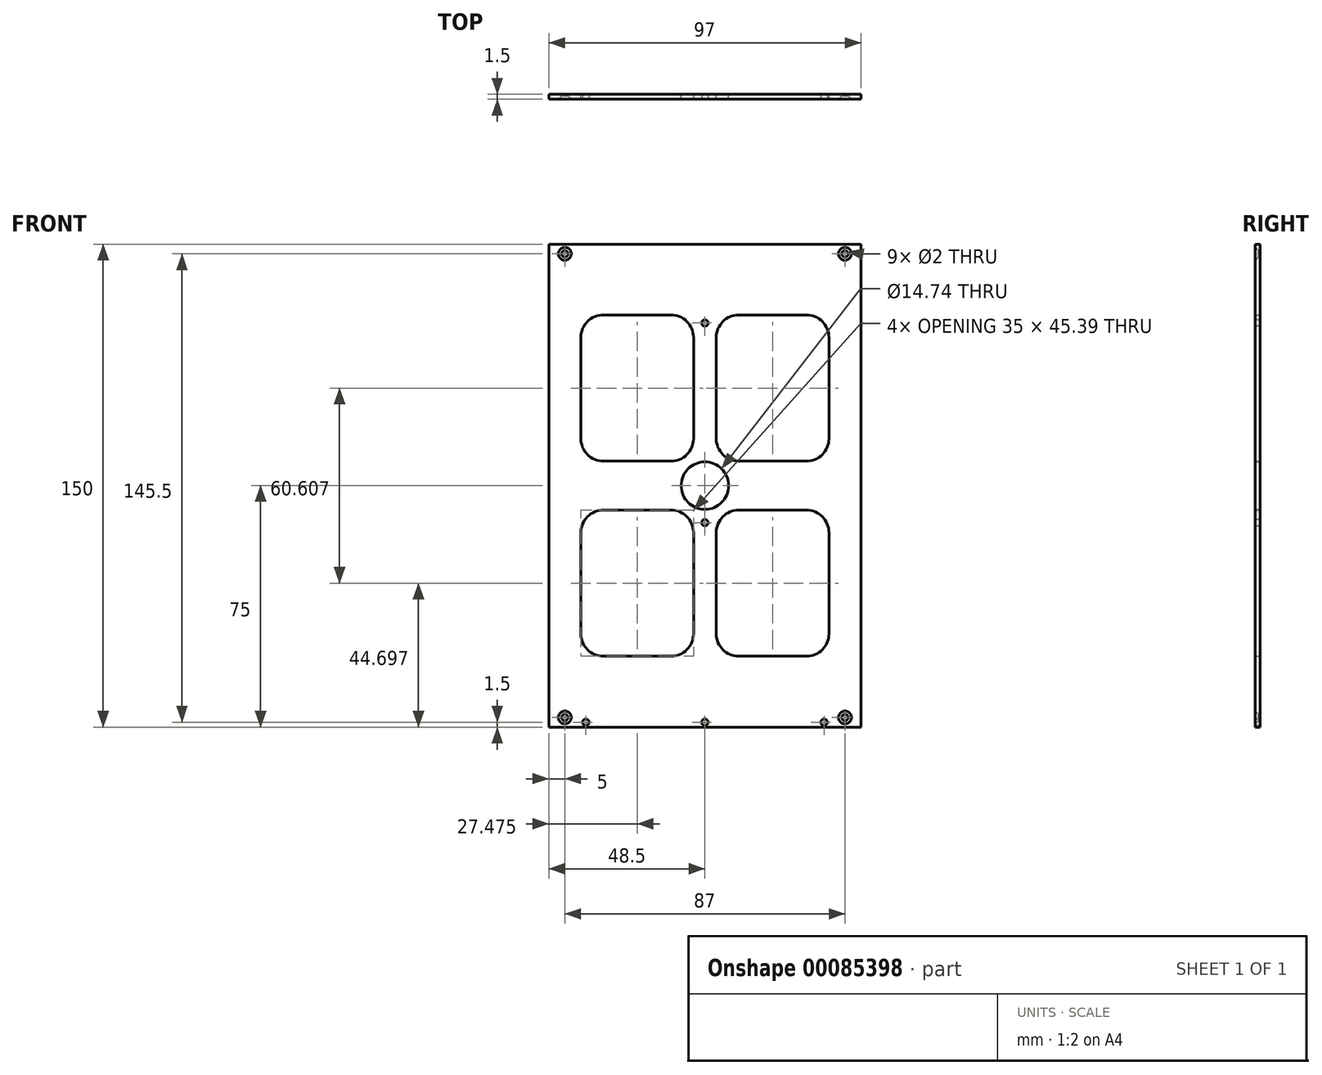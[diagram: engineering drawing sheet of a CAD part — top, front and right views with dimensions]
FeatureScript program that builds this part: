
annotation { "Feature Type Name" : "Feature", "Feature Type Description" : "" }
export const myFeature = defineFeature(function(context is Context, id is Id, definition is map)
    precondition{}
    {
        {
            var Q0;
            Q0=qCreatedBy(makeId("Front.planeOp"),FACE);
            var sketch = newSketch(context, id + "F0", { "sketchPlane" : qUnion([Q0])});
            skLineSegment(sketch, "E0.rect.bottom", {"start": v(-48.5, 75) * mm, "end": v(48.5, 75) * mm});
            skLineSegment(sketch, "E0.rect.top", {"start": v(-48.5, -75) * mm, "end": v(48.5, -75) * mm});
            skLineSegment(sketch, "E0.rect.left", {"start": v(-48.5, 75) * mm, "end": v(-48.5, -75) * mm});
            skLineSegment(sketch, "E0.rect.right", {"start": v(48.5, 75) * mm, "end": v(48.5, -75) * mm});
            skPoint(sketch, "E0.rect.middle", {"position": v(0, 0) * mm});
            skLineSegment(sketch, "E1.rect.bottom", {"start": v(-10.52, 7.6) * mm, "end": v(-31.52, 7.6) * mm});
            skLineSegment(sketch, "E1.rect.top", {"start": v(-10.52, 53) * mm, "end": v(-31.52, 53) * mm});
            skLineSegment(sketch, "E1.rect.left", {"start": v(-3.52, 14.6) * mm, "end": v(-3.52, 46) * mm});
            skLineSegment(sketch, "E1.rect.right", {"start": v(-38.52, 14.6) * mm, "end": v(-38.52, 46) * mm});
            skPoint(sketch, "E1.rect.middle", {"position": v(-21.02, 30.3) * mm});
            skPoint(sketch, "E2", {"position": v(0, 75) * mm});
            skPoint(sketch, "E3", {"position": v(-24.25, 75) * mm});
            skPoint(sketch, "E4.MirrorP", {"position": v(-24.25, -75) * mm});
            skPoint(sketch, "E5.visualSharp", {"position": v(-3.52, 7.6) * mm});
            skArc(sketch, "E5.filletArc", {"start": v(-10.52, 7.6) * mm, "mid": v(-5.58, 9.66) * mm, "end": v(-3.52, 14.6) * mm});
            skPoint(sketch, "E6.visualSharp", {"position": v(-3.52, 53) * mm});
            skArc(sketch, "E6.filletArc", {"start": v(-3.52, 46) * mm, "mid": v(-5.58, 50.95) * mm, "end": v(-10.52, 53) * mm});
            skPoint(sketch, "E7.visualSharp", {"position": v(-38.52, 53) * mm});
            skArc(sketch, "E7.filletArc", {"start": v(-31.52, 53) * mm, "mid": v(-36.47, 50.95) * mm, "end": v(-38.52, 46) * mm});
            skPoint(sketch, "E8.visualSharp", {"position": v(-38.52, 7.6) * mm});
            skArc(sketch, "E8.filletArc", {"start": v(-38.52, 14.6) * mm, "mid": v(-36.47, 9.66) * mm, "end": v(-31.52, 7.6) * mm});
            skLineSegment(sketch, "E9.MirrorCS", {"start": v(3.52, 14.6) * mm, "end": v(3.52, 46) * mm});
            skArc(sketch, "E10.MirrorCS", {"start": v(3.52, 46) * mm, "mid": v(5.58, 50.95) * mm, "end": v(10.52, 53) * mm});
            skLineSegment(sketch, "E11.MirrorCS", {"start": v(10.52, 53) * mm, "end": v(31.52, 53) * mm});
            skPoint(sketch, "E12.MirrorP", {"position": v(38.52, 53) * mm});
            skArc(sketch, "E13.MirrorCS", {"start": v(31.52, 53) * mm, "mid": v(36.47, 50.95) * mm, "end": v(38.52, 46) * mm});
            skLineSegment(sketch, "E14.MirrorCS", {"start": v(38.52, 14.6) * mm, "end": v(38.52, 46) * mm});
            skPoint(sketch, "E15.MirrorP", {"position": v(38.52, 7.6) * mm});
            skLineSegment(sketch, "E16.MirrorCS", {"start": v(10.52, 7.6) * mm, "end": v(31.52, 7.6) * mm});
            skArc(sketch, "E17.MirrorCS", {"start": v(38.52, 14.6) * mm, "mid": v(36.47, 9.66) * mm, "end": v(31.52, 7.6) * mm});
            skPoint(sketch, "E18.MirrorP", {"position": v(3.52, 7.6) * mm});
            skArc(sketch, "E19.MirrorCS", {"start": v(10.52, 7.6) * mm, "mid": v(5.58, 9.66) * mm, "end": v(3.52, 14.6) * mm});
            skPoint(sketch, "E20.MirrorP", {"position": v(3.52, 53) * mm});
            skArc(sketch, "E21.MirrorCS", {"start": v(31.52, -53) * mm, "mid": v(36.47, -50.95) * mm, "end": v(38.52, -46) * mm});
            skArc(sketch, "E22.MirrorCS", {"start": v(38.52, -14.6) * mm, "mid": v(36.47, -9.66) * mm, "end": v(31.52, -7.6) * mm});
            skArc(sketch, "E23.MirrorCS", {"start": v(10.52, -7.6) * mm, "mid": v(5.58, -9.66) * mm, "end": v(3.52, -14.6) * mm});
            skArc(sketch, "E24.MirrorCS", {"start": v(3.52, -46) * mm, "mid": v(5.58, -50.95) * mm, "end": v(10.52, -53) * mm});
            skPoint(sketch, "E25.MirrorP", {"position": v(38.52, -53) * mm});
            skLineSegment(sketch, "E26.MirrorCS", {"start": v(38.52, -14.6) * mm, "end": v(38.52, -46) * mm});
            skPoint(sketch, "E27.MirrorP", {"position": v(38.52, -7.6) * mm});
            skLineSegment(sketch, "E28.MirrorCS", {"start": v(3.52, -14.6) * mm, "end": v(3.52, -46) * mm});
            skPoint(sketch, "E29.MirrorP", {"position": v(3.52, -53) * mm});
            skLineSegment(sketch, "E30.MirrorCS", {"start": v(10.52, -7.6) * mm, "end": v(31.52, -7.6) * mm});
            skLineSegment(sketch, "E31.MirrorCS", {"start": v(10.52, -53) * mm, "end": v(31.52, -53) * mm});
            skPoint(sketch, "E32.MirrorP", {"position": v(3.52, -7.6) * mm});
            skArc(sketch, "E33.MirrorCS", {"start": v(-10.52, -7.6) * mm, "mid": v(-5.58, -9.66) * mm, "end": v(-3.52, -14.6) * mm});
            skArc(sketch, "E34.MirrorCS", {"start": v(-3.52, -46) * mm, "mid": v(-5.58, -50.95) * mm, "end": v(-10.52, -53) * mm});
            skArc(sketch, "E35.MirrorCS", {"start": v(-38.52, -14.6) * mm, "mid": v(-36.47, -9.66) * mm, "end": v(-31.52, -7.6) * mm});
            skArc(sketch, "E36.MirrorCS", {"start": v(-31.52, -53) * mm, "mid": v(-36.47, -50.95) * mm, "end": v(-38.52, -46) * mm});
            skPoint(sketch, "E37.MirrorP", {"position": v(-21.02, -30.3) * mm});
            skPoint(sketch, "E38.MirrorP", {"position": v(-3.52, -7.6) * mm});
            skPoint(sketch, "E39.MirrorP", {"position": v(-38.52, -53) * mm});
            skLineSegment(sketch, "E40.MirrorCS", {"start": v(-10.52, -7.6) * mm, "end": v(-31.52, -7.6) * mm});
            skLineSegment(sketch, "E41.MirrorCS", {"start": v(-10.52, -53) * mm, "end": v(-31.52, -53) * mm});
            skPoint(sketch, "E42.MirrorP", {"position": v(-3.52, -53) * mm});
            skLineSegment(sketch, "E43.MirrorCS", {"start": v(-3.52, -14.6) * mm, "end": v(-3.52, -46) * mm});
            skLineSegment(sketch, "E44.MirrorCS", {"start": v(-38.52, -14.6) * mm, "end": v(-38.52, -46) * mm});
            skPoint(sketch, "E45.MirrorP", {"position": v(-38.52, -7.6) * mm});
            skCircle(sketch, "E46", {"center": v(0, 0) * mm, "radius": 7.37 * mm});
            skSolve(sketch);
        }
        {
            var Q0;
            Q0=makeQuery(id+"F0.imprint","IMPRINT",FACE,{"disambiguationData":[TD([[makeQuery(id+"F0.imprint","IMPRINT",EDGE,{"derivedFrom":sQuery(id+"F0.wireOp",EDGE,"E0.rect.bottom")}),-1.0]])]});
            extrude(context, id + "F1", {"entities" : qUnion([Q0]), "depth" : 1.5 * mm});
        }
        {
            var Q0;
            Q0=makeQuery(id+"F1.opExtrude","CAP_FACE",FACE,{"disambiguationData":[OSD([sQuery(id+"F0.wireOp",EDGE,"E0.rect.bottom"),sQuery(id+"F0.wireOp",EDGE,"E0.rect.top"),sQuery(id+"F0.wireOp",EDGE,"E0.rect.left"),sQuery(id+"F0.wireOp",EDGE,"E0.rect.right"),sQuery(id+"F0.wireOp",EDGE,"E1.rect.bottom"),sQuery(id+"F0.wireOp",EDGE,"E1.rect.top"),sQuery(id+"F0.wireOp",EDGE,"E1.rect.left"),sQuery(id+"F0.wireOp",EDGE,"E1.rect.right"),sQuery(id+"F0.wireOp",EDGE,"E5.filletArc"),sQuery(id+"F0.wireOp",EDGE,"E6.filletArc"),sQuery(id+"F0.wireOp",EDGE,"E7.filletArc"),sQuery(id+"F0.wireOp",EDGE,"E8.filletArc"),sQuery(id+"F0.wireOp",EDGE,"E9.MirrorCS"),sQuery(id+"F0.wireOp",EDGE,"E10.MirrorCS"),sQuery(id+"F0.wireOp",EDGE,"E11.MirrorCS"),sQuery(id+"F0.wireOp",EDGE,"E13.MirrorCS"),sQuery(id+"F0.wireOp",EDGE,"E14.MirrorCS"),sQuery(id+"F0.wireOp",EDGE,"E16.MirrorCS"),sQuery(id+"F0.wireOp",EDGE,"E17.MirrorCS"),sQuery(id+"F0.wireOp",EDGE,"E19.MirrorCS"),sQuery(id+"F0.wireOp",EDGE,"E21.MirrorCS"),sQuery(id+"F0.wireOp",EDGE,"E22.MirrorCS"),sQuery(id+"F0.wireOp",EDGE,"E23.MirrorCS"),sQuery(id+"F0.wireOp",EDGE,"E24.MirrorCS"),sQuery(id+"F0.wireOp",EDGE,"E26.MirrorCS"),sQuery(id+"F0.wireOp",EDGE,"E28.MirrorCS"),sQuery(id+"F0.wireOp",EDGE,"E30.MirrorCS"),sQuery(id+"F0.wireOp",EDGE,"E31.MirrorCS"),sQuery(id+"F0.wireOp",EDGE,"E33.MirrorCS"),sQuery(id+"F0.wireOp",EDGE,"E34.MirrorCS"),sQuery(id+"F0.wireOp",EDGE,"E35.MirrorCS"),sQuery(id+"F0.wireOp",EDGE,"E36.MirrorCS"),sQuery(id+"F0.wireOp",EDGE,"E40.MirrorCS"),sQuery(id+"F0.wireOp",EDGE,"E41.MirrorCS"),sQuery(id+"F0.wireOp",EDGE,"E43.MirrorCS"),sQuery(id+"F0.wireOp",EDGE,"E44.MirrorCS"),sQuery(id+"F0.wireOp",EDGE,"deea28ce-c4f6-4fc3-8f0f-82602a925565.rect.bottom"),sQuery(id+"F0.wireOp",EDGE,"deea28ce-c4f6-4fc3-8f0f-82602a925565.rect.top"),sQuery(id+"F0.wireOp",EDGE,"deea28ce-c4f6-4fc3-8f0f-82602a925565.rect.left"),sQuery(id+"F0.wireOp",EDGE,"deea28ce-c4f6-4fc3-8f0f-82602a925565.rect.right"),sQuery(id+"F0.wireOp",EDGE,"92293470-82ba-44ad-9286-e8a1911384cd.filletArc"),sQuery(id+"F0.wireOp",EDGE,"f783d059-47c1-4597-a3b5-ce5ed20d1783.filletArc"),sQuery(id+"F0.wireOp",EDGE,"7d8a2005-66fb-4448-9a0b-17e6f11710ed.filletArc"),sQuery(id+"F0.wireOp",EDGE,"bd1f88c4-01d0-4c1f-b818-689555ed0d3d.filletArc"),sQuery(id+"F0.wireOp",EDGE,"3de75153-5ae1-45d4-89d9-6fcf70203f930.MirrorCS"),sQuery(id+"F0.wireOp",EDGE,"3de75153-5ae1-45d4-89d9-6fcf70203f931.MirrorCS"),sQuery(id+"F0.wireOp",EDGE,"3de75153-5ae1-45d4-89d9-6fcf70203f932.MirrorCS"),sQuery(id+"F0.wireOp",EDGE,"3de75153-5ae1-45d4-89d9-6fcf70203f933.MirrorCS"),sQuery(id+"F0.wireOp",EDGE,"3de75153-5ae1-45d4-89d9-6fcf70203f937.MirrorCS"),sQuery(id+"F0.wireOp",EDGE,"3de75153-5ae1-45d4-89d9-6fcf70203f939.MirrorCS"),sQuery(id+"F0.wireOp",EDGE,"3de75153-5ae1-45d4-89d9-6fcf70203f9311.MirrorCS"),sQuery(id+"F0.wireOp",EDGE,"3de75153-5ae1-45d4-89d9-6fcf70203f9312.MirrorCS")])],"isStart":false});
            var sketch = newSketch(context, id + "F2", { "sketchPlane" : qUnion([Q0])});
            skPoint(sketch, "E47", {"position": v(-43.5, -72) * mm});
            skPoint(sketch, "E48.MirrorP", {"position": v(43.5, -72) * mm});
            skPoint(sketch, "E49.MirrorP", {"position": v(-43.5, 72) * mm});
            skPoint(sketch, "E50.MirrorP", {"position": v(43.5, 72) * mm});
            skSolve(sketch);
        }
        {
            var Q0;
            Q0=sQuery(id+"F2.wireOp",VERTEX,"E47");
            var Q1;
            Q1=sQuery(id+"F2.wireOp",VERTEX,"E48.MirrorP");
            var Q2;
            Q2=sQuery(id+"F2.wireOp",VERTEX,"E50.MirrorP");
            var Q3;
            Q3=sQuery(id+"F2.wireOp",VERTEX,"E49.MirrorP");
            var Q4;
            Q4=sQuery(id+"F2.wireOp",VERTEX,"f692f96d-b3ef-4b25-bd05-95c4abe1053b");
            var Q5;
            Q5=sQuery(id+"F2.wireOp",VERTEX,"6fb1c37c-decf-44f5-8bba-7a2e60b1c09a");
            var Q6;
            Q6=sQuery(id+"F2.wireOp",VERTEX,"e5432b45-bd6c-42e0-96c4-d4a1cdefc3be");
            var Q7;
            Q7=sQuery(id+"F2.wireOp",VERTEX,"cf76a1ca-a373-4096-b586-4708a9325641");
            var Q8;
            Q8=sQuery(id+"F2.wireOp",VERTEX,"19e9ac87-c4db-4f84-8793-d0dcfe6b89480.MirrorP");
            var Q9;
            Q9=sQuery(id+"F2.wireOp",VERTEX,"cf40c92d-3cb4-4fd1-9011-2b1b11cf86800.MirrorP");
            var Q10;
            Q10=sQuery(id+"F2.wireOp",VERTEX,"dbe2afd2-cc13-4726-9d4e-a7426feb8f1a0.MirrorP");
            var Q11;
            Q11=sQuery(id+"F2.wireOp",VERTEX,"da7565b5-0760-4871-9ab9-0602c46f39720.MirrorP");
            var Q12;
            Q12=sQuery(id+"F2.wireOp",VERTEX,"17fecccd-3962-452f-9978-7328e825eee30.MirrorP");
            var Q13;
            Q13=sQuery(id+"F2.wireOp",VERTEX,"4bd07c42-14cb-4c0a-9484-79320a5c3db60.MirrorP");
            var Q14;
            Q14=sQuery(id+"F2.wireOp",VERTEX,"4bebc43e-6cee-4dba-a944-25e79cf908630.MirrorP");
            var Q15;
            Q15=sQuery(id+"F2.wireOp",VERTEX,"e56d2771-9223-44ee-8796-3a5c91e851be0.MirrorP");
            var Q16;
            Q16=sQuery(id+"F2.wireOp",VERTEX,"fc323023-5ca8-47af-bc60-2d4e8e6fe2a30.MirrorP");
            var Q17;
            Q17=sQuery(id+"F2.wireOp",VERTEX,"0839c29d-2d7f-409f-b01c-e3268e62f07b0.MirrorP");
            var Q18;
            Q18=sQuery(id+"F2.wireOp",VERTEX,"a23aa490-2248-47f4-872f-093390e742580.MirrorP");
            var Q19;
            Q19=sQuery(id+"F2.wireOp",VERTEX,"f29489ae-a8f8-488d-b8ee-71de4e1048c30.MirrorP");
            var Q20;
            Q20=makeQuery(id+"F1.opExtrude","SWEPT_BODY",BODY,{"disambiguationData":[OSD([sQuery(id+"F0.wireOp",EDGE,"E0.rect.bottom"),sQuery(id+"F0.wireOp",EDGE,"E0.rect.top"),sQuery(id+"F0.wireOp",EDGE,"E0.rect.left"),sQuery(id+"F0.wireOp",EDGE,"E0.rect.right"),sQuery(id+"F0.wireOp",EDGE,"E1.rect.bottom"),sQuery(id+"F0.wireOp",EDGE,"E1.rect.top"),sQuery(id+"F0.wireOp",EDGE,"E1.rect.left"),sQuery(id+"F0.wireOp",EDGE,"E1.rect.right"),sQuery(id+"F0.wireOp",EDGE,"E5.filletArc"),sQuery(id+"F0.wireOp",EDGE,"E6.filletArc"),sQuery(id+"F0.wireOp",EDGE,"E7.filletArc"),sQuery(id+"F0.wireOp",EDGE,"E8.filletArc"),sQuery(id+"F0.wireOp",EDGE,"E9.MirrorCS"),sQuery(id+"F0.wireOp",EDGE,"E10.MirrorCS"),sQuery(id+"F0.wireOp",EDGE,"E11.MirrorCS"),sQuery(id+"F0.wireOp",EDGE,"E13.MirrorCS"),sQuery(id+"F0.wireOp",EDGE,"E14.MirrorCS"),sQuery(id+"F0.wireOp",EDGE,"E16.MirrorCS"),sQuery(id+"F0.wireOp",EDGE,"E17.MirrorCS"),sQuery(id+"F0.wireOp",EDGE,"E19.MirrorCS"),sQuery(id+"F0.wireOp",EDGE,"E21.MirrorCS"),sQuery(id+"F0.wireOp",EDGE,"E22.MirrorCS"),sQuery(id+"F0.wireOp",EDGE,"E23.MirrorCS"),sQuery(id+"F0.wireOp",EDGE,"E24.MirrorCS"),sQuery(id+"F0.wireOp",EDGE,"E26.MirrorCS"),sQuery(id+"F0.wireOp",EDGE,"E28.MirrorCS"),sQuery(id+"F0.wireOp",EDGE,"E30.MirrorCS"),sQuery(id+"F0.wireOp",EDGE,"E31.MirrorCS"),sQuery(id+"F0.wireOp",EDGE,"E33.MirrorCS"),sQuery(id+"F0.wireOp",EDGE,"E34.MirrorCS"),sQuery(id+"F0.wireOp",EDGE,"E35.MirrorCS"),sQuery(id+"F0.wireOp",EDGE,"E36.MirrorCS"),sQuery(id+"F0.wireOp",EDGE,"E40.MirrorCS"),sQuery(id+"F0.wireOp",EDGE,"E41.MirrorCS"),sQuery(id+"F0.wireOp",EDGE,"E43.MirrorCS"),sQuery(id+"F0.wireOp",EDGE,"E44.MirrorCS"),sQuery(id+"F0.wireOp",EDGE,"deea28ce-c4f6-4fc3-8f0f-82602a925565.rect.bottom"),sQuery(id+"F0.wireOp",EDGE,"deea28ce-c4f6-4fc3-8f0f-82602a925565.rect.top"),sQuery(id+"F0.wireOp",EDGE,"deea28ce-c4f6-4fc3-8f0f-82602a925565.rect.left"),sQuery(id+"F0.wireOp",EDGE,"deea28ce-c4f6-4fc3-8f0f-82602a925565.rect.right"),sQuery(id+"F0.wireOp",EDGE,"92293470-82ba-44ad-9286-e8a1911384cd.filletArc"),sQuery(id+"F0.wireOp",EDGE,"f783d059-47c1-4597-a3b5-ce5ed20d1783.filletArc"),sQuery(id+"F0.wireOp",EDGE,"7d8a2005-66fb-4448-9a0b-17e6f11710ed.filletArc"),sQuery(id+"F0.wireOp",EDGE,"bd1f88c4-01d0-4c1f-b818-689555ed0d3d.filletArc"),sQuery(id+"F0.wireOp",EDGE,"3de75153-5ae1-45d4-89d9-6fcf70203f930.MirrorCS"),sQuery(id+"F0.wireOp",EDGE,"3de75153-5ae1-45d4-89d9-6fcf70203f931.MirrorCS"),sQuery(id+"F0.wireOp",EDGE,"3de75153-5ae1-45d4-89d9-6fcf70203f932.MirrorCS"),sQuery(id+"F0.wireOp",EDGE,"3de75153-5ae1-45d4-89d9-6fcf70203f933.MirrorCS"),sQuery(id+"F0.wireOp",EDGE,"3de75153-5ae1-45d4-89d9-6fcf70203f937.MirrorCS"),sQuery(id+"F0.wireOp",EDGE,"3de75153-5ae1-45d4-89d9-6fcf70203f939.MirrorCS"),sQuery(id+"F0.wireOp",EDGE,"3de75153-5ae1-45d4-89d9-6fcf70203f9311.MirrorCS"),sQuery(id+"F0.wireOp",EDGE,"3de75153-5ae1-45d4-89d9-6fcf70203f9312.MirrorCS")])]});
            hole(context, id + "F3", {"style" : HoleStyle.C_SINK, "holeDiameter" : 2 * mm, "cSinkDiameter" : 4 * mm, "endStyle" : HoleEndStyle.THROUGH, "locations" : qUnion([Q0, Q1, Q2, Q3, Q4, Q5, Q6, Q7, Q8, Q9, Q10, Q11, Q12, Q13, Q14, Q15, Q16, Q17, Q18, Q19]), "scope" : qUnion([Q20]), "cSinkAngle" : 90 * degree, "isTappedThrough" : true});
        }
        {
            var Q0;
            Q0=makeQuery(id+"F1.opExtrude","CAP_FACE",FACE,{"disambiguationData":[OSD([sQuery(id+"F0.wireOp",EDGE,"E0.rect.bottom"),sQuery(id+"F0.wireOp",EDGE,"E0.rect.top"),sQuery(id+"F0.wireOp",EDGE,"E0.rect.left"),sQuery(id+"F0.wireOp",EDGE,"E0.rect.right"),sQuery(id+"F0.wireOp",EDGE,"E1.rect.bottom"),sQuery(id+"F0.wireOp",EDGE,"E1.rect.top"),sQuery(id+"F0.wireOp",EDGE,"E1.rect.left"),sQuery(id+"F0.wireOp",EDGE,"E1.rect.right"),sQuery(id+"F0.wireOp",EDGE,"E5.filletArc"),sQuery(id+"F0.wireOp",EDGE,"E6.filletArc"),sQuery(id+"F0.wireOp",EDGE,"E7.filletArc"),sQuery(id+"F0.wireOp",EDGE,"E8.filletArc"),sQuery(id+"F0.wireOp",EDGE,"E9.MirrorCS"),sQuery(id+"F0.wireOp",EDGE,"E10.MirrorCS"),sQuery(id+"F0.wireOp",EDGE,"E11.MirrorCS"),sQuery(id+"F0.wireOp",EDGE,"E13.MirrorCS"),sQuery(id+"F0.wireOp",EDGE,"E14.MirrorCS"),sQuery(id+"F0.wireOp",EDGE,"E16.MirrorCS"),sQuery(id+"F0.wireOp",EDGE,"E17.MirrorCS"),sQuery(id+"F0.wireOp",EDGE,"E19.MirrorCS"),sQuery(id+"F0.wireOp",EDGE,"E21.MirrorCS"),sQuery(id+"F0.wireOp",EDGE,"E22.MirrorCS"),sQuery(id+"F0.wireOp",EDGE,"E23.MirrorCS"),sQuery(id+"F0.wireOp",EDGE,"E24.MirrorCS"),sQuery(id+"F0.wireOp",EDGE,"E26.MirrorCS"),sQuery(id+"F0.wireOp",EDGE,"E28.MirrorCS"),sQuery(id+"F0.wireOp",EDGE,"E30.MirrorCS"),sQuery(id+"F0.wireOp",EDGE,"E31.MirrorCS"),sQuery(id+"F0.wireOp",EDGE,"E33.MirrorCS"),sQuery(id+"F0.wireOp",EDGE,"E34.MirrorCS"),sQuery(id+"F0.wireOp",EDGE,"E35.MirrorCS"),sQuery(id+"F0.wireOp",EDGE,"E36.MirrorCS"),sQuery(id+"F0.wireOp",EDGE,"E40.MirrorCS"),sQuery(id+"F0.wireOp",EDGE,"E41.MirrorCS"),sQuery(id+"F0.wireOp",EDGE,"E43.MirrorCS"),sQuery(id+"F0.wireOp",EDGE,"E44.MirrorCS"),sQuery(id+"F0.wireOp",EDGE,"E46")])],"isStart":false});
            var sketch = newSketch(context, id + "F4", { "sketchPlane" : qUnion([Q0])});
            skCircle(sketch, "E51", {"center": v(-37, -73.5) * mm, "radius": 1 * mm});
            skCircle(sketch, "E52.0.1.0", {"center": v(-37, -11.5) * mm, "radius": 1 * mm});
            skCircle(sketch, "E52.0.2.0", {"center": v(-37, 50.5) * mm, "radius": 1 * mm});
            skCircle(sketch, "E52.1.0.0", {"center": v(0, -73.5) * mm, "radius": 1 * mm});
            skCircle(sketch, "E52.1.1.0", {"center": v(0, -11.5) * mm, "radius": 1 * mm});
            skCircle(sketch, "E52.1.2.0", {"center": v(0, 50.5) * mm, "radius": 1 * mm});
            skCircle(sketch, "E52.2.0.0", {"center": v(37, -73.5) * mm, "radius": 1 * mm});
            skCircle(sketch, "E52.2.1.0", {"center": v(37, -11.5) * mm, "radius": 1 * mm});
            skCircle(sketch, "E52.2.2.0", {"center": v(37, 50.5) * mm, "radius": 1 * mm});
            skLineSegment(sketch, "E52.direction1", {"start": v(-37, -73.5) * mm, "end": v(0, -73.5) * mm, "construction": true});
            skLineSegment(sketch, "E52.direction2", {"start": v(-37, -73.5) * mm, "end": v(-37, -11.5) * mm, "construction": true});
            skSolve(sketch);
        }
        {
            var Q0;
            Q0=sQuery(id+"F4.wireOp",VERTEX,"E51.center");
            var Q1;
            Q1=sQuery(id+"F4.wireOp",VERTEX,"E52.1.0.0.center");
            var Q2;
            Q2=sQuery(id+"F4.wireOp",VERTEX,"E52.2.0.0.center");
            var Q3;
            Q3=sQuery(id+"F4.wireOp",VERTEX,"E52.1.1.0.center");
            var Q4;
            Q4=sQuery(id+"F4.wireOp",VERTEX,"E52.1.2.0.center");
            var Q5;
            Q5=makeQuery(id+"F1.opExtrude","SWEPT_BODY",BODY,{"disambiguationData":[OSD([sQuery(id+"F0.wireOp",EDGE,"E0.rect.bottom"),sQuery(id+"F0.wireOp",EDGE,"E0.rect.top"),sQuery(id+"F0.wireOp",EDGE,"E0.rect.left"),sQuery(id+"F0.wireOp",EDGE,"E0.rect.right"),sQuery(id+"F0.wireOp",EDGE,"E1.rect.bottom"),sQuery(id+"F0.wireOp",EDGE,"E1.rect.top"),sQuery(id+"F0.wireOp",EDGE,"E1.rect.left"),sQuery(id+"F0.wireOp",EDGE,"E1.rect.right"),sQuery(id+"F0.wireOp",EDGE,"E5.filletArc"),sQuery(id+"F0.wireOp",EDGE,"E6.filletArc"),sQuery(id+"F0.wireOp",EDGE,"E7.filletArc"),sQuery(id+"F0.wireOp",EDGE,"E8.filletArc"),sQuery(id+"F0.wireOp",EDGE,"E9.MirrorCS"),sQuery(id+"F0.wireOp",EDGE,"E10.MirrorCS"),sQuery(id+"F0.wireOp",EDGE,"E11.MirrorCS"),sQuery(id+"F0.wireOp",EDGE,"E13.MirrorCS"),sQuery(id+"F0.wireOp",EDGE,"E14.MirrorCS"),sQuery(id+"F0.wireOp",EDGE,"E16.MirrorCS"),sQuery(id+"F0.wireOp",EDGE,"E17.MirrorCS"),sQuery(id+"F0.wireOp",EDGE,"E19.MirrorCS"),sQuery(id+"F0.wireOp",EDGE,"E21.MirrorCS"),sQuery(id+"F0.wireOp",EDGE,"E22.MirrorCS"),sQuery(id+"F0.wireOp",EDGE,"E23.MirrorCS"),sQuery(id+"F0.wireOp",EDGE,"E24.MirrorCS"),sQuery(id+"F0.wireOp",EDGE,"E26.MirrorCS"),sQuery(id+"F0.wireOp",EDGE,"E28.MirrorCS"),sQuery(id+"F0.wireOp",EDGE,"E30.MirrorCS"),sQuery(id+"F0.wireOp",EDGE,"E31.MirrorCS"),sQuery(id+"F0.wireOp",EDGE,"E33.MirrorCS"),sQuery(id+"F0.wireOp",EDGE,"E34.MirrorCS"),sQuery(id+"F0.wireOp",EDGE,"E35.MirrorCS"),sQuery(id+"F0.wireOp",EDGE,"E36.MirrorCS"),sQuery(id+"F0.wireOp",EDGE,"E40.MirrorCS"),sQuery(id+"F0.wireOp",EDGE,"E41.MirrorCS"),sQuery(id+"F0.wireOp",EDGE,"E43.MirrorCS"),sQuery(id+"F0.wireOp",EDGE,"E44.MirrorCS"),sQuery(id+"F0.wireOp",EDGE,"E46")])]});
            hole(context, id + "F5", {"style" : HoleStyle.SIMPLE, "endStyle" : HoleEndStyle.THROUGH, "holeDiameter" : 2 * mm, "locations" : qUnion([Q0, Q1, Q2, Q3, Q4]), "scope" : qUnion([Q5]), "isTappedThrough" : true});
        }
    });
